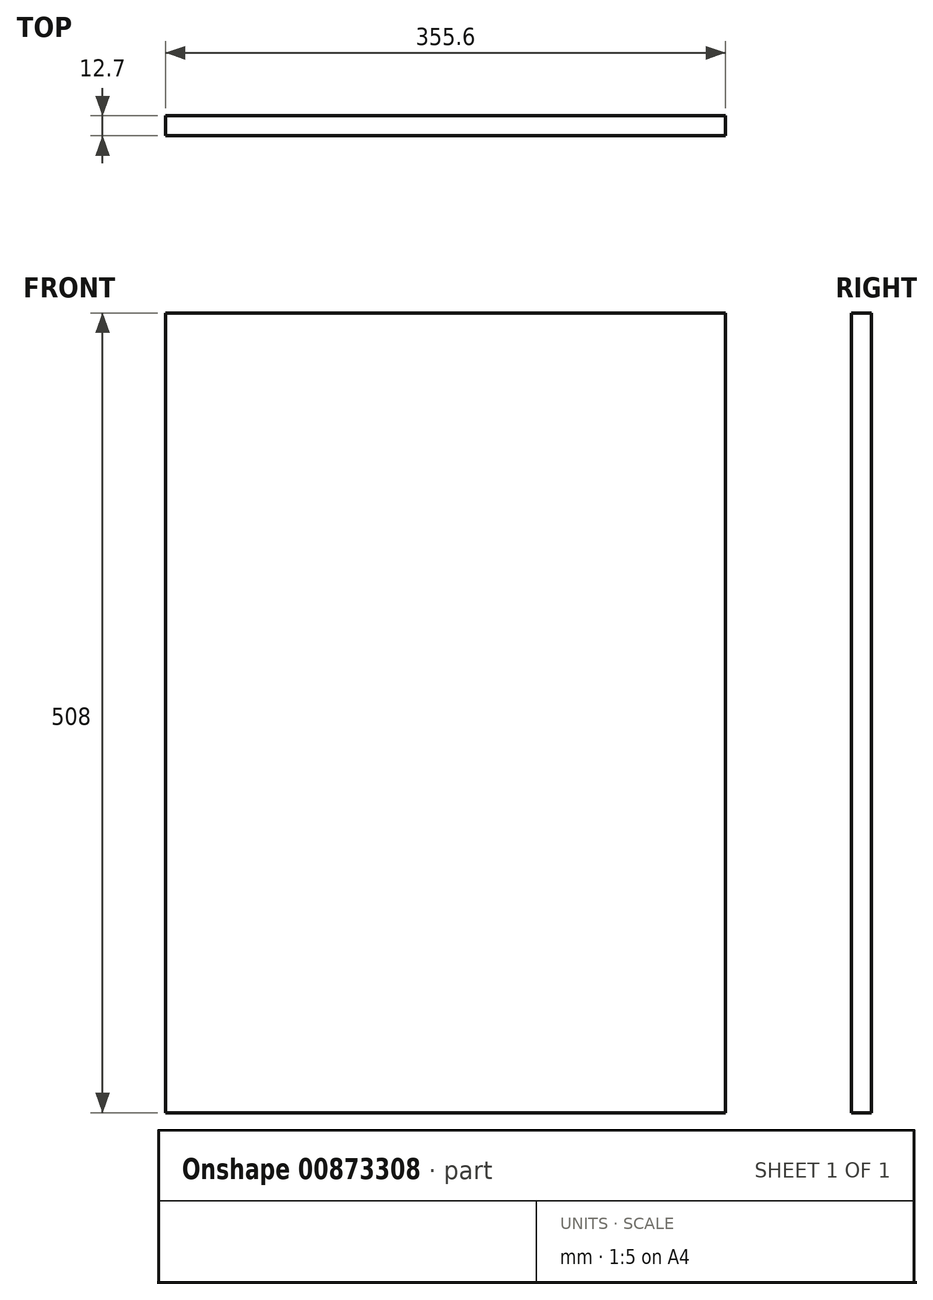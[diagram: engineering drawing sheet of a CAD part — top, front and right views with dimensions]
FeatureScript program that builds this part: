
annotation { "Feature Type Name" : "Feature", "Feature Type Description" : "" }
export const myFeature = defineFeature(function(context is Context, id is Id, definition is map)
    precondition{}
    {
        {
            var Q0;
            Q0=qCreatedBy(makeId("Front.planeOp"),FACE);
            var sketch = newSketch(context, id + "F0", { "sketchPlane" : qUnion([Q0])});
            skLineSegment(sketch, "E0.bottom", {"start": v(0, 0) * mm, "end": v(-355.6, 0) * mm});
            skLineSegment(sketch, "E0.top", {"start": v(0, 508) * mm, "end": v(-355.6, 508) * mm});
            skLineSegment(sketch, "E0.left", {"start": v(0, 0) * mm, "end": v(0, 508) * mm});
            skLineSegment(sketch, "E0.right", {"start": v(-355.6, 0) * mm, "end": v(-355.6, 508) * mm});
            skSolve(sketch);
        }
        {
            var Q0;
            Q0=makeQuery(id+"F0.imprint","IMPRINT",FACE,{"disambiguationData":[TD([[makeQuery(id+"F0.imprint","IMPRINT",EDGE,{"derivedFrom":sQuery(id+"F0.wireOp",EDGE,"E0.bottom")}),-1.0]])]});
            extrude(context, id + "F1", {"entities" : qUnion([Q0]), "depth" : 12.7 * mm, "offsetDistance" : 25.4 * mm});
        }
    });
